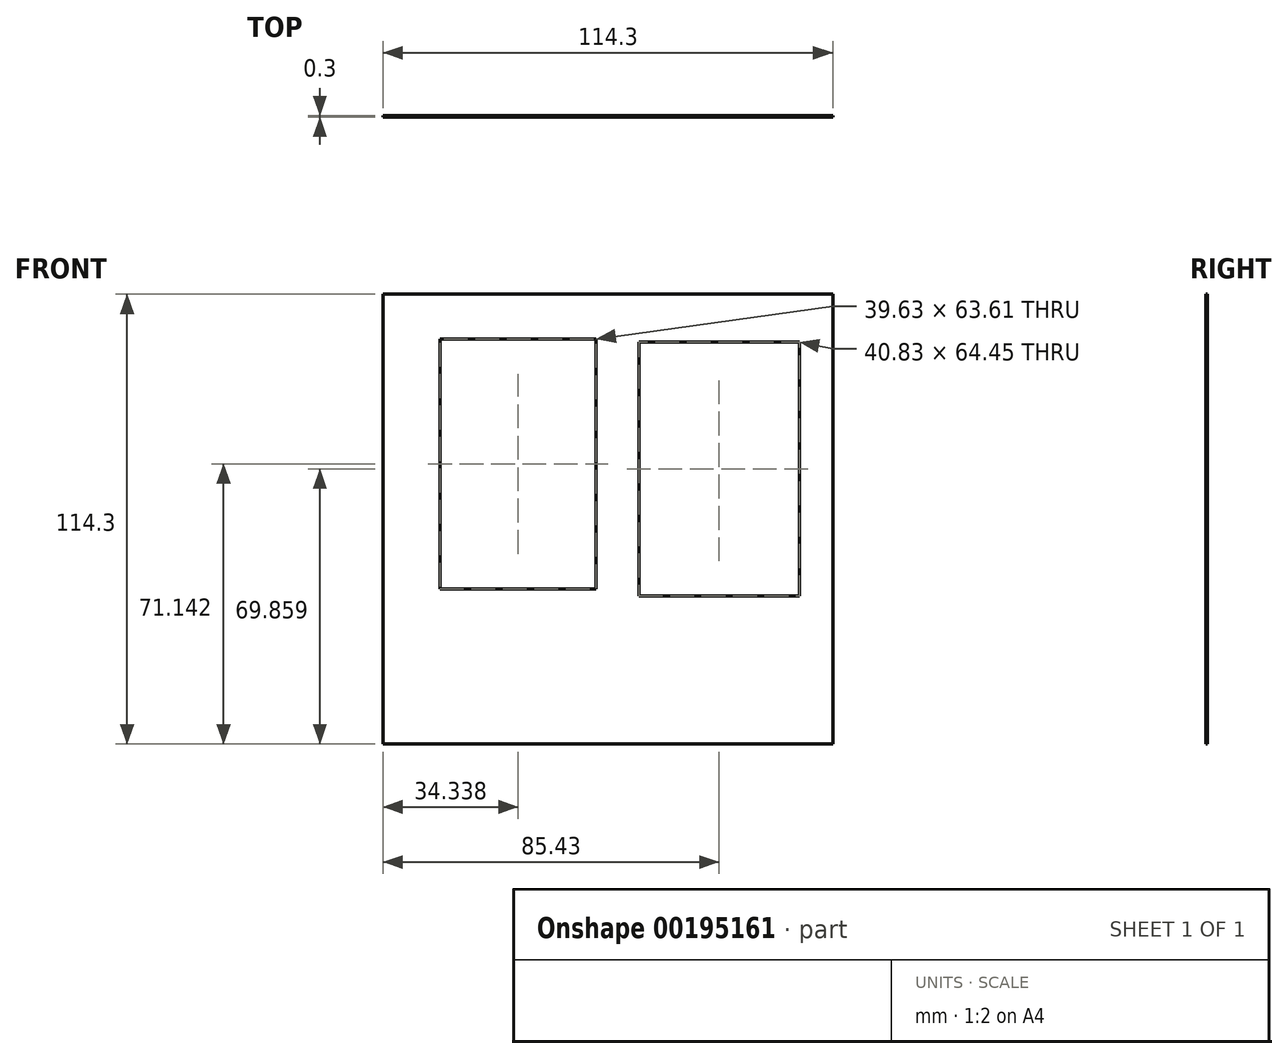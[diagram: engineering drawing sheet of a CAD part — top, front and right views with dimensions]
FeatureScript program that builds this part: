
annotation { "Feature Type Name" : "Feature", "Feature Type Description" : "" }
export const myFeature = defineFeature(function(context is Context, id is Id, definition is map)
    precondition{}
    {
        {
            var Q0;
            Q0=qCreatedBy(makeId("Front.planeOp"),FACE);
            var sketch = newSketch(context, id + "F0", { "sketchPlane" : qUnion([Q0])});
            skLineSegment(sketch, "E0.bottom", {"start": v(-50.32, 63.95) * mm, "end": v(63.98, 63.95) * mm});
            skLineSegment(sketch, "E0.top", {"start": v(-50.32, -50.35) * mm, "end": v(63.98, -50.35) * mm});
            skLineSegment(sketch, "E0.left", {"start": v(-50.32, 63.95) * mm, "end": v(-50.32, -50.35) * mm});
            skLineSegment(sketch, "E0.right", {"start": v(63.98, 63.95) * mm, "end": v(63.98, -50.35) * mm});
            skSolve(sketch);
        }
        {
            var Q0;
            Q0=makeQuery(id+"F0.imprint","IMPRINT",FACE,{"disambiguationData":[TD([[makeQuery(id+"F0.imprint","IMPRINT",EDGE,{"derivedFrom":sQuery(id+"F0.wireOp",EDGE,"E0.bottom")}),-1.0]])]});
            extrude(context, id + "F1", {"entities" : qUnion([Q0]), "depth" : 0.3 * mm});
        }
        {
            var Q0;
            Q0=makeQuery(id+"F1.opExtrude","CAP_FACE",FACE,{"disambiguationData":[OSD([sQuery(id+"F0.wireOp",EDGE,"E0.bottom"),sQuery(id+"F0.wireOp",EDGE,"E0.top"),sQuery(id+"F0.wireOp",EDGE,"E0.left"),sQuery(id+"F0.wireOp",EDGE,"E0.right")])],"isStart":false});
            var sketch = newSketch(context, id + "F2", { "sketchPlane" : qUnion([Q0])});
            skLineSegment(sketch, "E1.bottom", {"start": v(-35.8, 52.6) * mm, "end": v(3.83, 52.6) * mm});
            skLineSegment(sketch, "E1.top", {"start": v(-35.8, -11.02) * mm, "end": v(3.83, -11.02) * mm});
            skLineSegment(sketch, "E1.left", {"start": v(-35.8, 52.6) * mm, "end": v(-35.8, -11.02) * mm});
            skLineSegment(sketch, "E1.right", {"start": v(3.83, 52.6) * mm, "end": v(3.83, -11.02) * mm});
            skSolve(sketch);
        }
        {
            var Q0;
            Q0 = qSketchRegion(id + "F2", true);
            extrude(context, id + "F3", {"entities" : qUnion([Q0]), "operationType" : NewBodyOperationType.REMOVE, "endBound" : BoundingType.THROUGH_ALL, "oppositeDirection" : true, "depth" : 25.4 * mm});
        }
        {
            var Q0;
            Q0=makeQuery(id+"F1.opExtrude","CAP_FACE",FACE,{"disambiguationData":[OSD([sQuery(id+"F0.wireOp",EDGE,"E0.bottom"),sQuery(id+"F0.wireOp",EDGE,"E0.top"),sQuery(id+"F0.wireOp",EDGE,"E0.left"),sQuery(id+"F0.wireOp",EDGE,"E0.right")])],"isStart":false});
            var sketch = newSketch(context, id + "F4", { "sketchPlane" : qUnion([Q0])});
            skLineSegment(sketch, "E2.bottom", {"start": v(14.7, 51.74) * mm, "end": v(55.53, 51.74) * mm});
            skLineSegment(sketch, "E2.top", {"start": v(14.7, -12.72) * mm, "end": v(55.53, -12.72) * mm});
            skLineSegment(sketch, "E2.left", {"start": v(14.7, 51.74) * mm, "end": v(14.7, -12.72) * mm});
            skLineSegment(sketch, "E2.right", {"start": v(55.53, 51.74) * mm, "end": v(55.53, -12.72) * mm});
            skSolve(sketch);
        }
        {
            var Q0;
            Q0 = qSketchRegion(id + "F4", true);
            extrude(context, id + "F5", {"entities" : qUnion([Q0]), "operationType" : NewBodyOperationType.REMOVE, "endBound" : BoundingType.THROUGH_ALL, "oppositeDirection" : true, "depth" : 25.4 * mm});
        }
    });
